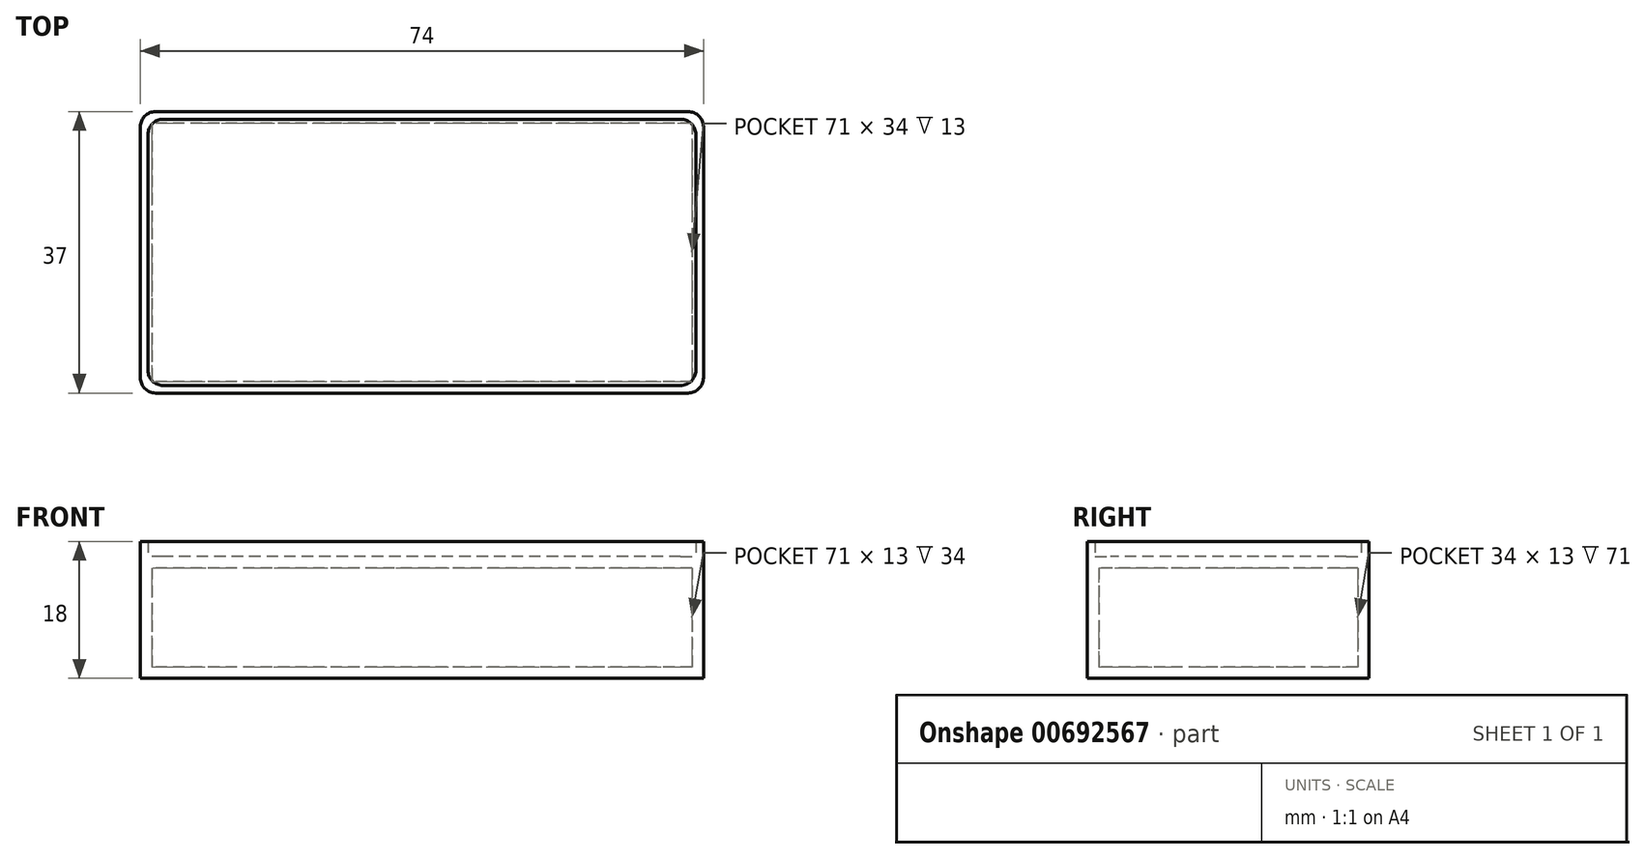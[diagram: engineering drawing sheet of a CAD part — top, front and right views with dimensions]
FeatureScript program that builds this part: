
annotation { "Feature Type Name" : "Feature", "Feature Type Description" : "" }
export const myFeature = defineFeature(function(context is Context, id is Id, definition is map)
    precondition{}
    {
        {
            var Q0;
            Q0=qCreatedBy(makeId("Top.planeOp"),FACE);
            var sketch = newSketch(context, id + "F0", { "sketchPlane" : qUnion([Q0])});
            skLineSegment(sketch, "E0.bottom", {"start": v(37, 18.5) * mm, "end": v(-37, 18.5) * mm});
            skLineSegment(sketch, "E0.top", {"start": v(37, -18.5) * mm, "end": v(-37, -18.5) * mm});
            skLineSegment(sketch, "E0.left", {"start": v(37, 18.5) * mm, "end": v(37, -18.5) * mm});
            skLineSegment(sketch, "E0.right", {"start": v(-37, 18.5) * mm, "end": v(-37, -18.5) * mm});
            skPoint(sketch, "E0.middle", {"position": v(0, 0) * mm});
            skSolve(sketch);
        }
        {
            var Q0;
            Q0=makeQuery(id+"F0.imprint","IMPRINT",FACE,{"disambiguationData":[TD([[makeQuery(id+"F0.imprint","IMPRINT",EDGE,{"derivedFrom":sQuery(id+"F0.wireOp",EDGE,"E0.bottom")}),1.0]])]});
            extrude(context, id + "F1", {"entities" : qUnion([Q0]), "depth" : 16 * mm, "offsetDistance" : 25 * mm});
        }
        {
            var Q0;
            Q0=makeQuery(id+"F1.opExtrude","CAP_FACE",FACE,{"disambiguationData":[OSD([sQuery(id+"F0.wireOp",EDGE,"E0.bottom"),sQuery(id+"F0.wireOp",EDGE,"E0.top"),sQuery(id+"F0.wireOp",EDGE,"E0.left"),sQuery(id+"F0.wireOp",EDGE,"E0.right")])],"isStart":false});
            var Q1;
            Q1=makeQuery(id+"F1.opExtrude","SWEPT_BODY",BODY,{"disambiguationData":[OSD([sQuery(id+"F0.wireOp",EDGE,"E0.bottom"),sQuery(id+"F0.wireOp",EDGE,"E0.top"),sQuery(id+"F0.wireOp",EDGE,"E0.left"),sQuery(id+"F0.wireOp",EDGE,"E0.right")])]});
            shell(context, id + "F2", {"isHollow" : true, "entities" : qUnion([Q0]), "parts" : qUnion([Q1]), "thickness" : 1.5 * mm});
        }
        {
            var Q0;
            Q0=makeQuery(id+"F1.opExtrude","CAP_FACE",FACE,{"disambiguationData":[OSD([sQuery(id+"F0.wireOp",EDGE,"E0.bottom"),sQuery(id+"F0.wireOp",EDGE,"E0.top"),sQuery(id+"F0.wireOp",EDGE,"E0.left"),sQuery(id+"F0.wireOp",EDGE,"E0.right")])],"isStart":false});
            var sketch = newSketch(context, id + "F3", { "sketchPlane" : qUnion([Q0])});
            skLineSegment(sketch, "E1.bottom", {"start": v(36, 17.5) * mm, "end": v(-36, 17.5) * mm});
            skLineSegment(sketch, "E1.top", {"start": v(36, -17.5) * mm, "end": v(-36, -17.5) * mm});
            skLineSegment(sketch, "E1.left", {"start": v(36, 17.5) * mm, "end": v(36, -17.5) * mm});
            skLineSegment(sketch, "E1.right", {"start": v(-36, 17.5) * mm, "end": v(-36, -17.5) * mm});
            skPoint(sketch, "E1.middle", {"position": v(0, 0) * mm});
            skSolve(sketch);
        }
        {
            var Q0;
            Q0=makeQuery(id+"F3.imprint","IMPRINT",FACE,{"disambiguationData":[TD([[makeQuery(id+"F3.imprint","IMPRINT",EDGE,{"derivedFrom":sQuery(id+"F3.wireOp",EDGE,"E1.bottom")}),-1.0]])]});
            extrude(context, id + "F4", {"entities" : qUnion([Q0]), "operationType" : NewBodyOperationType.ADD, "depth" : 2 * mm, "offsetDistance" : 25 * mm});
        }
        {
            var Q0;
            {var subQ0=sQuery(id+"F0.wireOp",EDGE,"E0.right");var subQ1=sQuery(id+"F0.wireOp",EDGE,"E0.top");Q0=makeQuery(id+"F4.boolean.opBoolean","MERGE",EDGE,{"derivedFrom":[makeQuery(id+"F1.opExtrude","SWEPT_EDGE",EDGE,{"disambiguationData":[OSD([subQ1,subQ0])]}),makeQuery(id+"F4.opExtrude","SWEPT_EDGE",EDGE,{"disambiguationData":[OSD([subQ1,subQ0])]})]});}
            var Q1;
            Q1=makeQuery(id+"F4.opExtrude","SWEPT_EDGE",EDGE,{"disambiguationData":[OSD([sQuery(id+"F3.wireOp",EDGE,"E1.bottom"),sQuery(id+"F3.wireOp",EDGE,"E1.left")])]});
            var Q2;
            Q2=makeQuery(id+"F4.opExtrude","SWEPT_EDGE",EDGE,{"disambiguationData":[OSD([sQuery(id+"F3.wireOp",EDGE,"E1.bottom"),sQuery(id+"F3.wireOp",EDGE,"E1.right")])]});
            var Q3;
            Q3=makeQuery(id+"F4.opExtrude","SWEPT_EDGE",EDGE,{"disambiguationData":[OSD([sQuery(id+"F3.wireOp",EDGE,"E1.top"),sQuery(id+"F3.wireOp",EDGE,"E1.right")])]});
            var Q4;
            Q4=makeQuery(id+"F4.opExtrude","SWEPT_EDGE",EDGE,{"disambiguationData":[OSD([sQuery(id+"F3.wireOp",EDGE,"E1.top"),sQuery(id+"F3.wireOp",EDGE,"E1.left")])]});
            var Q5;
            {var subQ0=sQuery(id+"F0.wireOp",EDGE,"E0.left");var subQ1=sQuery(id+"F0.wireOp",EDGE,"E0.top");Q5=makeQuery(id+"F4.boolean.opBoolean","MERGE",EDGE,{"derivedFrom":[makeQuery(id+"F1.opExtrude","SWEPT_EDGE",EDGE,{"disambiguationData":[OSD([subQ1,subQ0])]}),makeQuery(id+"F4.opExtrude","SWEPT_EDGE",EDGE,{"disambiguationData":[OSD([subQ1,subQ0])]})]});}
            var Q6;
            {var subQ0=sQuery(id+"F0.wireOp",EDGE,"E0.right");var subQ1=sQuery(id+"F0.wireOp",EDGE,"E0.bottom");Q6=makeQuery(id+"F4.boolean.opBoolean","MERGE",EDGE,{"derivedFrom":[makeQuery(id+"F1.opExtrude","SWEPT_EDGE",EDGE,{"disambiguationData":[OSD([subQ1,subQ0])]}),makeQuery(id+"F4.opExtrude","SWEPT_EDGE",EDGE,{"disambiguationData":[OSD([subQ1,subQ0])]})]});}
            var Q7;
            {var subQ0=sQuery(id+"F0.wireOp",EDGE,"E0.left");var subQ1=sQuery(id+"F0.wireOp",EDGE,"E0.bottom");Q7=makeQuery(id+"F4.boolean.opBoolean","MERGE",EDGE,{"derivedFrom":[makeQuery(id+"F1.opExtrude","SWEPT_EDGE",EDGE,{"disambiguationData":[OSD([subQ1,subQ0])]}),makeQuery(id+"F4.opExtrude","SWEPT_EDGE",EDGE,{"disambiguationData":[OSD([subQ1,subQ0])]})]});}
            fillet(context, id + "F5", {"entities" : qUnion([Q0, Q1, Q2, Q3, Q4, Q5, Q6, Q7]), "radius" : 2 * mm, "tangentPropagation" : true, "allowEdgeOverflow" : false});
        }
    });
